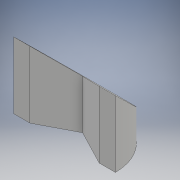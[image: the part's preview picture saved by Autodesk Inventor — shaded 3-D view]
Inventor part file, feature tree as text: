
AUTODESK INVENTOR PART (.ipt)
format: ipt  version: 2018 (Build 220112000, 112)  size: 113,152 bytes
history: native  units: mm
features: sketch x2, extrude x2
ambient origin geometry x8: Origin, YZ Plane, XZ Plane, XY Plane, X Axis, Y Axis, Z Axis, Center Point
bodies: Solid1 (feature_tree)
feature tree (4):
  sketch  "Sketch1"  dims[d0=9.25mm d1=9.25mm]
  sketch  "Sketch2"  dims[d2=14.25mm d3=4.5mm d6=4.5mm d7=4.5mm d8=14.125mm d9=5.0mm d10=28.25mm d11=0.0mm d12=50.0mm d13=50.0mm d14=28.25mm d15=0.0mm]
  extrude  "Extrusion1"  Depth=9.25mm
  extrude  "Extrusion2"  Depth=5.0mm
